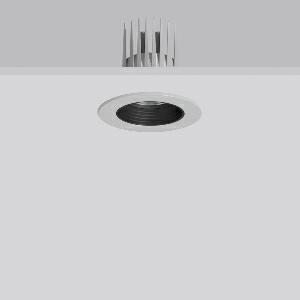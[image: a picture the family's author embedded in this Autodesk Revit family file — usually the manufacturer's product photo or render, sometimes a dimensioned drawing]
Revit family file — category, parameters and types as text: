
# Revit family: heledon_mini_e_901746_004_3_76_e79c
name_source: partatom
category: Lighting Fixtures
units: mm (PartAtom-declared; Revit-internal decimal feet)

## family parameters
Cut with Voids When Loaded = No
Host = Face
Light Source = No
Part Type = Normal
Room Calculation Point = No
Round Connector Dimension = Use Diameter
Shared = No

## types (1)
- HELEDON mini E (1 x LED Modul 935, 2300 lm, 3500)
    Apparent Load = 20 VA
    Approval mark = CE
    CIE Flux Codes = 80 99 100 100 100
    Color Rendering = 92
    Color Temperature = 3500
    Default Elevation = 1800 mm
    Description = Series: HELEDON mini
Round recessed downlight. Housing: die-cast aluminium, powder-coated. Black plastic ring and recessed LED to prevent glare from the side. Optical assembly with lens made of plastic (polycarbonate) for the best homogeneous light distribution - can be changed without tools. Best colour rendering index Ra>90. Suitable for Recessed ceiling mounting. Installation without tools thanks to spring fastening system. Including separate LED converter with connecting cable 600 mm.High quality converter without flickering and stroboscopic effect. Through-wiring box (5 pole) available as accessory. The following accessories can be mounted without use of tools: interchangeable lenses, decorative glasses, honeycomb louvre, clear and frosted diffusers, white interchangeable plastic ring. 
Colour: silver
Diameter: 124 mm
Height: 3 mm
Cut-out diameter: 114 mm
Recess height: 170 mm
Luminaire: recess height: 120 mm
Lamp: LED
Socket: without socket
Colour temperature: 3500K
Colour rendering index (CRI): 92
System power: 20 W
Rated luminous flux: 2300 lm
Luminous efficiency: 115 lm/W
Control gear: Converter, dimmable, DALI
Protection class: II
Type of protection: IP 20
    Height = 0 mm  [stored 0 ft]
    Lamp = 1 x LED Modul 935
    Lamp Light Flux = 2300 lm
    Lamp count = 1
    Length = 124 mm  [stored 0.406824 ft]
    Lifetime = 50000 h
    Luminous efficacy = 115 lm/W
    Manufacturer = RZB
    ModVariant = No
    Model = 901746.004.3.76
    Mounting Place = Ceiling
    Mounting Type = Recessed
    Number of Poles = 1
    OnlyDefault = Yes
    Power Factor = 1
    Product Name = HELEDON mini E
    Product group = Recessed downlights
    ProductGroupID = 402
    Protection Class = Protection class II
    Protection Degree = IP 20
    RLX_Detail_Level = 1
    RLX_Emergency_Light_Flux = 0 lm
    RLX_Emergency_Type = 0
    RLX_Emergency_Type_DB = No
    RlxData = <blob elided: 126561 chars, md5=3af2bd71>
    Socket = socket
    Standby Power = 0 W
    System Light Flux = 2300 lm
    System Power = 20 W
    Type Comments = Product without accessories
    Type Image = 901656.004.jpg
    URL = http://relux.com
    VarID = ---
    Voltage = 230 V
    Voltage Range = 220-240 V
    Weight = 0.00 kg
    Width = 0 mm  [stored 0 ft]

note: [stored X ft] marks values corroborated as IEEE doubles in the binary element streams (Revit-internal decimal feet)

## geometry (parser evidence)
native form markers: Blend x4, Sweep x10
no freeform markers — native parametric forms only
